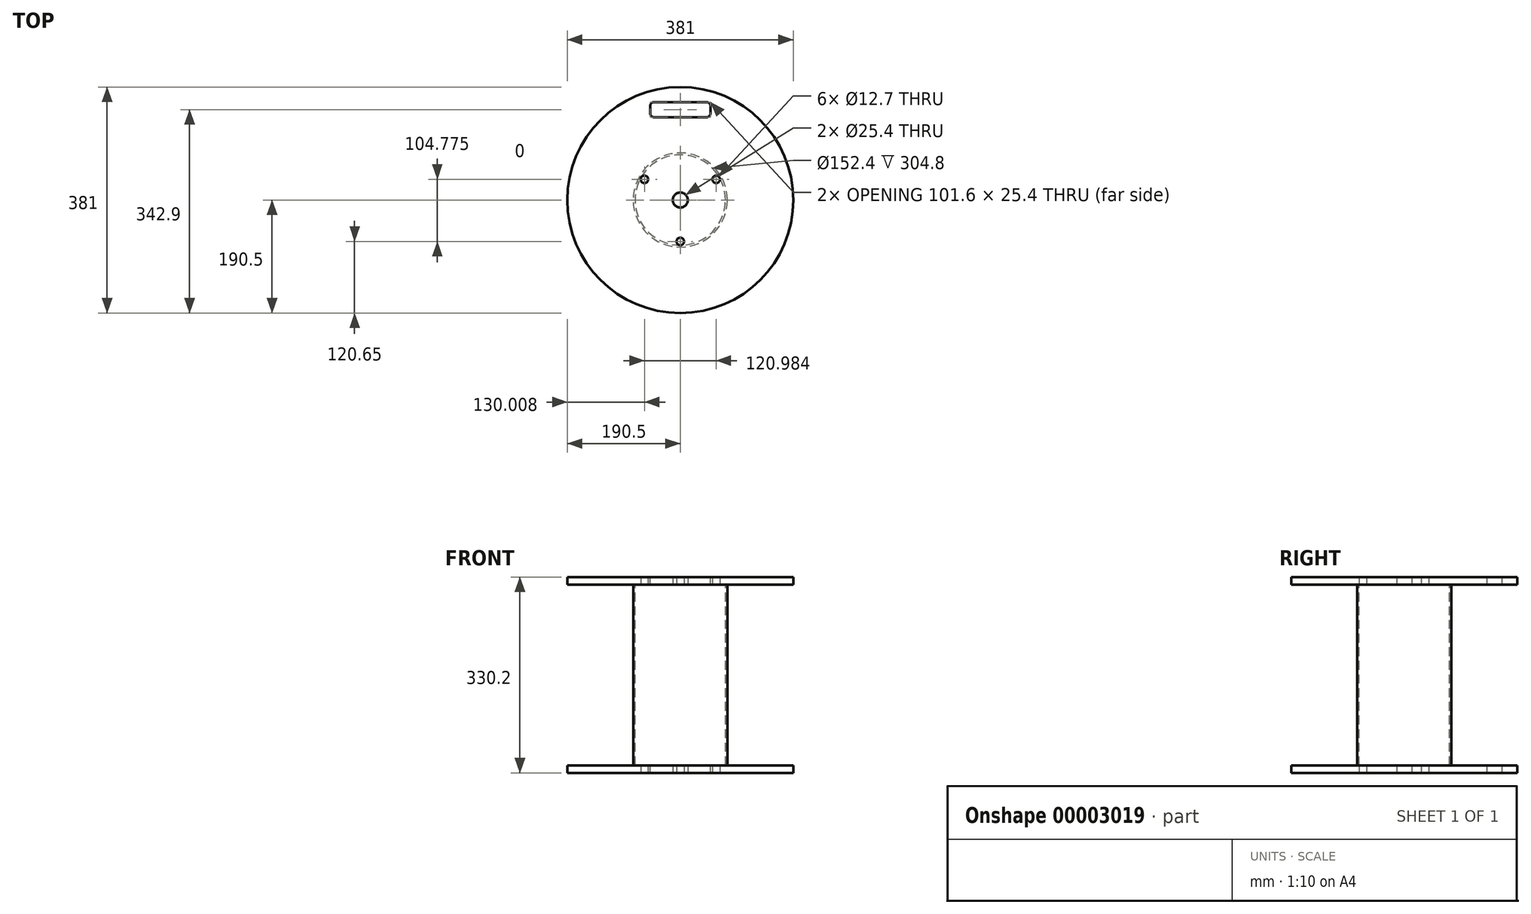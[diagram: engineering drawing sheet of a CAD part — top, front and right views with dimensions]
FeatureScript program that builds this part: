
annotation { "Feature Type Name" : "Feature", "Feature Type Description" : "" }
export const myFeature = defineFeature(function(context is Context, id is Id, definition is map)
    precondition{}
    {
        {
            var Q0;
            Q0=qCreatedBy(makeId("Top.planeOp"),FACE);
            var sketch = newSketch(context, id + "F0", { "sketchPlane" : qUnion([Q0])});
            skCircle(sketch, "E0", {"center": v(0, 0) * mm, "radius": 190.5 * mm});
            skSolve(sketch);
        }
        {
            var Q0;
            Q0=makeQuery(id+"F0.imprint","IMPRINT",FACE,{"disambiguationData":[TD([[makeQuery(id+"F0.imprint","IMPRINT",EDGE,{"derivedFrom":sQuery(id+"F0.wireOp",EDGE,"E0")}),1.0]])]});
            extrude(context, id + "F1", {"entities" : qUnion([Q0]), "depth" : 12.7 * mm});
        }
        {
            var Q0;
            Q0=makeQuery(id+"F1.opExtrude","CAP_FACE",FACE,{"disambiguationData":[OSD([sQuery(id+"F0.wireOp",EDGE,"E0")])],"isStart":true});
            cPlane(context, id + "F2", {"entities" : qUnion([Q0]), "cplaneType" : CPlaneType.OFFSET, "offset" : 304.8 * mm, "width" : 152.4 * mm, "height" : 152.4 * mm});
        }
        {
            var Q0;
            Q0=qCreatedBy(id+"F2.planeOp",FACE);
            var sketch = newSketch(context, id + "F3", { "sketchPlane" : qUnion([Q0])});
            skCircle(sketch, "E1.0.0", {"center": v(0, 0) * mm, "radius": 190.5 * mm});
            skSolve(sketch);
        }
        {
            var Q0;
            Q0=makeQuery(id+"F3.imprint","IMPRINT",FACE,{"disambiguationData":[TD([[makeQuery(id+"F3.imprint","IMPRINT",EDGE,{"derivedFrom":sQuery(id+"F3.wireOp",EDGE,"E1.0.0")}),1.0]])]});
            extrude(context, id + "F4", {"entities" : qUnion([Q0]), "depth" : 12.7 * mm});
        }
        {
            var Q0;
            Q0=makeQuery(id+"F1.opExtrude","CAP_FACE",FACE,{"disambiguationData":[OSD([sQuery(id+"F0.wireOp",EDGE,"E0")])],"isStart":true});
            var sketch = newSketch(context, id + "F5", { "sketchPlane" : qUnion([Q0])});
            skCircle(sketch, "E2", {"center": v(0, 0) * mm, "radius": 76.2 * mm});
            skCircle(sketch, "E3.0", {"center": v(0, 0) * mm, "radius": 79.38 * mm});
            skCircle(sketch, "E4.0", {"center": v(0, 0) * mm, "radius": 184.15 * mm});
            skSolve(sketch);
        }
        {
            var Q0;
            Q0=makeQuery(id+"F5.imprint","IMPRINT",FACE,{"disambiguationData":[TD([[makeQuery(id+"F5.imprint","IMPRINT",EDGE,{"derivedFrom":sQuery(id+"F5.wireOp",EDGE,"E2")}),-1.0]])]});
            var Q1;
            Q1=makeQuery(id+"F4.opExtrude","CAP_FACE",FACE,{"disambiguationData":[OSD([sQuery(id+"F3.wireOp",EDGE,"E1.0.0")])],"isStart":true});
            extrude(context, id + "F6", {"entities" : qUnion([Q0]), "endBound" : BoundingType.UP_TO_SURFACE, "endBoundEntityFace" : qUnion([Q1]), "depth" : 25.4 * mm});
        }
        {
            var Q0;
            Q0=makeQuery(id+"F4.opExtrude","CAP_FACE",FACE,{"disambiguationData":[OSD([sQuery(id+"F3.wireOp",EDGE,"E1.0.0")])],"isStart":false});
            var sketch = newSketch(context, id + "F7", { "sketchPlane" : qUnion([Q0])});
            skCircle(sketch, "E5", {"center": v(0, 0) * mm, "radius": 76.2 * mm});
            skCircle(sketch, "E6", {"center": v(0, 69.85) * mm, "radius": 6.35 * mm});
            skLineSegment(sketch, "E7", {"start": v(0, 0) * mm, "end": v(0, 76.2) * mm, "construction": true});
            skLineSegment(sketch, "E8", {"start": v(66, -38.1) * mm, "end": v(0, 0) * mm, "construction": true});
            skLineSegment(sketch, "E9", {"start": v(-66, -38.1) * mm, "end": v(0, 0) * mm, "construction": true});
            skCircle(sketch, "E10", {"center": v(-60.5, -34.92) * mm, "radius": 6.35 * mm});
            skCircle(sketch, "E11", {"center": v(60.5, -34.92) * mm, "radius": 6.35 * mm});
            skSolve(sketch);
        }
        {
            var Q0;
            Q0=makeQuery(id+"F7.imprint","IMPRINT",FACE,{"disambiguationData":[TD([[makeQuery(id+"F7.imprint","IMPRINT",EDGE,{"derivedFrom":sQuery(id+"F7.wireOp",EDGE,"E6")}),1.0]])]});
            var Q1;
            Q1=makeQuery(id+"F7.imprint","IMPRINT",FACE,{"disambiguationData":[TD([[makeQuery(id+"F7.imprint","IMPRINT",EDGE,{"derivedFrom":sQuery(id+"F7.wireOp",EDGE,"E11")}),1.0]])]});
            var Q2;
            Q2=makeQuery(id+"F7.imprint","IMPRINT",FACE,{"disambiguationData":[TD([[makeQuery(id+"F7.imprint","IMPRINT",EDGE,{"derivedFrom":sQuery(id+"F7.wireOp",EDGE,"E10")}),1.0]])]});
            extrude(context, id + "F8", {"entities" : qUnion([Q0, Q1, Q2]), "operationType" : NewBodyOperationType.REMOVE, "endBound" : BoundingType.THROUGH_ALL, "oppositeDirection" : true, "depth" : 25.4 * mm});
        }
        {
            var Q0;
            Q0=makeQuery(id+"F4.opExtrude","CAP_FACE",FACE,{"disambiguationData":[OSD([sQuery(id+"F3.wireOp",EDGE,"E1.0.0")])],"isStart":false});
            var sketch = newSketch(context, id + "F9", { "sketchPlane" : qUnion([Q0])});
            skCircle(sketch, "E12", {"center": v(0, 0) * mm, "radius": 12.7 * mm});
            skSolve(sketch);
        }
        {
            var Q0;
            Q0=makeQuery(id+"F9.imprint","IMPRINT",FACE,{"disambiguationData":[TD([[makeQuery(id+"F9.imprint","IMPRINT",EDGE,{"derivedFrom":sQuery(id+"F9.wireOp",EDGE,"E12")}),1.0]])]});
            extrude(context, id + "F10", {"entities" : qUnion([Q0]), "operationType" : NewBodyOperationType.REMOVE, "endBound" : BoundingType.THROUGH_ALL, "oppositeDirection" : true, "depth" : 25.4 * mm});
        }
        {
            var Q0;
            Q0=makeQuery(id+"F1.opExtrude","CAP_FACE",FACE,{"disambiguationData":[OSD([sQuery(id+"F0.wireOp",EDGE,"E0")])],"isStart":false});
            var sketch = newSketch(context, id + "F11", { "sketchPlane" : qUnion([Q0])});
            skLineSegment(sketch, "E13.bottom", {"start": v(-44.45, 165.1) * mm, "end": v(44.45, 165.1) * mm});
            skLineSegment(sketch, "E13.top", {"start": v(-44.45, 139.7) * mm, "end": v(44.45, 139.7) * mm});
            skLineSegment(sketch, "E13.left", {"start": v(-50.8, 158.75) * mm, "end": v(-50.8, 146.05) * mm});
            skLineSegment(sketch, "E13.right", {"start": v(50.8, 158.75) * mm, "end": v(50.8, 146.05) * mm});
            skPoint(sketch, "E14.visualSharp", {"position": v(-50.8, 165.1) * mm});
            skArc(sketch, "E14.filletArc", {"start": v(-44.45, 165.1) * mm, "mid": v(-48.94, 163.24) * mm, "end": v(-50.8, 158.75) * mm});
            skPoint(sketch, "E15.visualSharp", {"position": v(-50.8, 139.7) * mm});
            skArc(sketch, "E15.filletArc", {"start": v(-50.8, 146.05) * mm, "mid": v(-48.94, 141.56) * mm, "end": v(-44.45, 139.7) * mm});
            skPoint(sketch, "E16.visualSharp", {"position": v(50.8, 165.1) * mm});
            skArc(sketch, "E16.filletArc", {"start": v(50.8, 158.75) * mm, "mid": v(48.94, 163.24) * mm, "end": v(44.45, 165.1) * mm});
            skPoint(sketch, "E17.visualSharp", {"position": v(50.8, 139.7) * mm});
            skArc(sketch, "E17.filletArc", {"start": v(44.45, 139.7) * mm, "mid": v(48.94, 141.56) * mm, "end": v(50.8, 146.05) * mm});
            skSolve(sketch);
        }
        {
            var Q0;
            Q0=makeQuery(id+"F11.imprint","IMPRINT",FACE,{"disambiguationData":[TD([[makeQuery(id+"F11.imprint","IMPRINT",EDGE,{"derivedFrom":sQuery(id+"F11.wireOp",EDGE,"E13.bottom")}),-1.0]])]});
            extrude(context, id + "F12", {"entities" : qUnion([Q0]), "operationType" : NewBodyOperationType.REMOVE, "endBound" : BoundingType.THROUGH_ALL, "oppositeDirection" : true, "depth" : 25.4 * mm});
        }
    });
